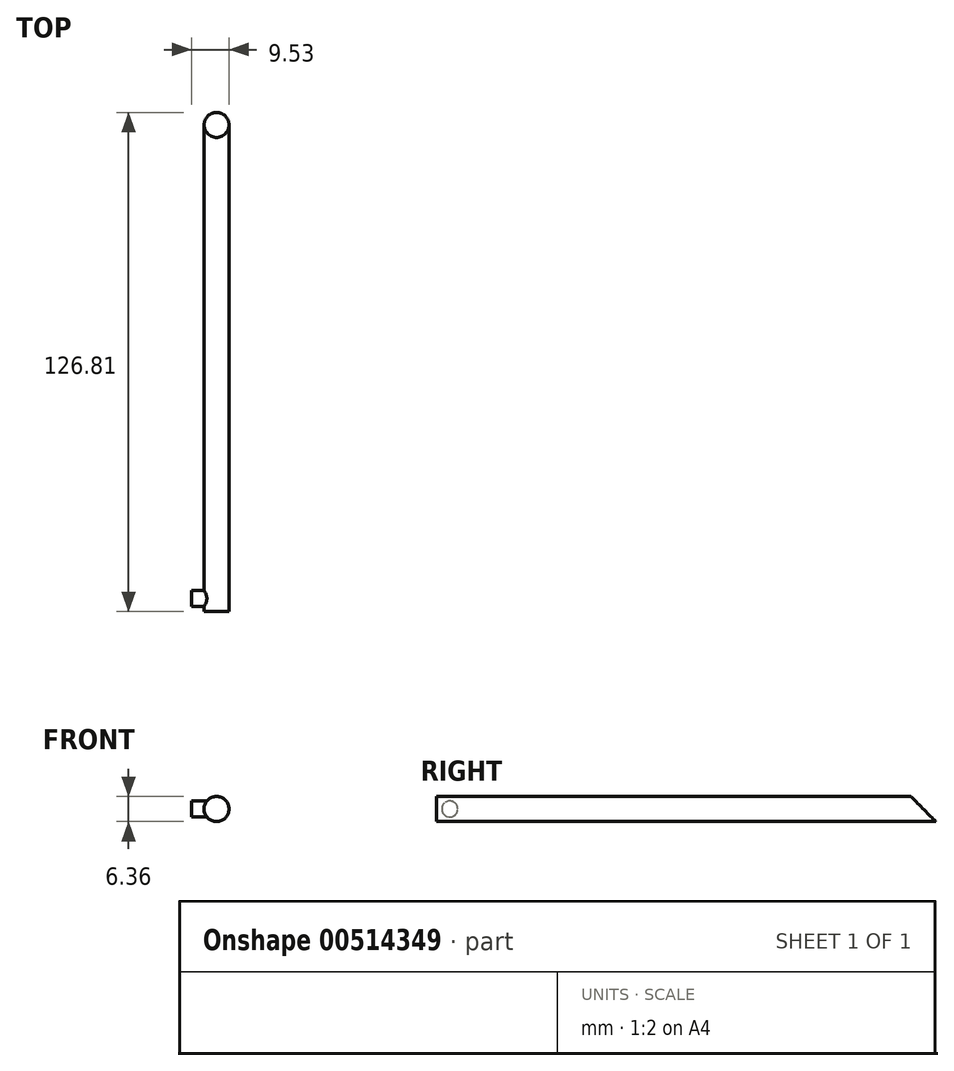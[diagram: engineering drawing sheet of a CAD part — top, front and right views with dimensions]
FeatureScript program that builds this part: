
annotation { "Feature Type Name" : "Feature", "Feature Type Description" : "" }
export const myFeature = defineFeature(function(context is Context, id is Id, definition is map)
    precondition{}
    {
        {
            var Q0;
            Q0=qCreatedBy(makeId("Front.planeOp"),FACE);
            var sketch = newSketch(context, id + "F0", { "sketchPlane" : qUnion([Q0])});
            skCircle(sketch, "E0", {"center": v(0, 0) * mm, "radius": 3.18 * mm});
            skSolve(sketch);
        }
        {
            var Q0;
            Q0=makeQuery(id+"F0.imprint","IMPRINT",FACE,{"disambiguationData":[TD([[makeQuery(id+"F0.imprint","IMPRINT",EDGE,{"derivedFrom":sQuery(id+"F0.wireOp",EDGE,"E0")}),1.0]])]});
            var Q1;
            Q1=sQuery(id+"F0.wireOp",EDGE,"E0");
            extrude(context, id + "F1", {"entities" : qUnion([Q0]), "surfaceEntities" : qUnion([Q1]), "depth" : 127 * mm});
        }
        {
            var Q0;
            Q0=qCreatedBy(makeId("Right.planeOp"),FACE);
            var sketch = newSketch(context, id + "F2", { "sketchPlane" : qUnion([Q0])});
            skCircle(sketch, "E1", {"center": v(-123.69, 0) * mm, "radius": 2.03 * mm});
            skSolve(sketch);
        }
        {
            var Q0;
            Q0=makeQuery(id+"F2.imprint","IMPRINT",FACE,{"disambiguationData":[TD([[makeQuery(id+"F2.imprint","IMPRINT",EDGE,{"derivedFrom":sQuery(id+"F2.wireOp",EDGE,"E1")}),1.0]])]});
            var Q1;
            Q1=sQuery(id+"F2.wireOp",EDGE,"E1");
            extrude(context, id + "F3", {"entities" : qUnion([Q0]), "operationType" : NewBodyOperationType.ADD, "surfaceEntities" : qUnion([Q1]), "oppositeDirection" : true, "depth" : 6.35 * mm});
        }
        {
            var Q0;
            Q0=qCreatedBy(makeId("Right.planeOp"),FACE);
            var sketch = newSketch(context, id + "F4", { "sketchPlane" : qUnion([Q0])});
            skLineSegment(sketch, "E2", {"start": v(0.15, 3.56) * mm, "end": v(0.15, -3.52) * mm});
            skLineSegment(sketch, "E3", {"start": v(0.15, -3.52) * mm, "end": v(-6.93, 3.56) * mm});
            skLineSegment(sketch, "E4", {"start": v(-6.93, 3.56) * mm, "end": v(0.15, 3.56) * mm});
            skLineSegment(sketch, "E5.bottom", {"start": v(0, 0) * mm, "end": v(-6.02, 0) * mm, "construction": true});
            skLineSegment(sketch, "E5.top", {"start": v(0, -3.18) * mm, "end": v(-6.02, -3.18) * mm, "construction": true});
            skLineSegment(sketch, "E5.left", {"start": v(0, 0) * mm, "end": v(0, -3.18) * mm, "construction": true});
            skLineSegment(sketch, "E5.right", {"start": v(-6.02, 0) * mm, "end": v(-6.02, -3.18) * mm, "construction": true});
            skSolve(sketch);
        }
        {
            var Q0;
            Q0=makeQuery(id+"F4.imprint","IMPRINT",FACE,{"disambiguationData":[TD([[makeQuery(id+"F4.imprint","IMPRINT",EDGE,{"derivedFrom":sQuery(id+"F4.wireOp",EDGE,"E2")}),-1.0]])]});
            extrude(context, id + "F5", {"entities" : qUnion([Q0]), "operationType" : NewBodyOperationType.REMOVE, "endBound" : BoundingType.SYMMETRIC, "oppositeDirection" : true, "depth" : 25.4 * mm});
        }
    });
